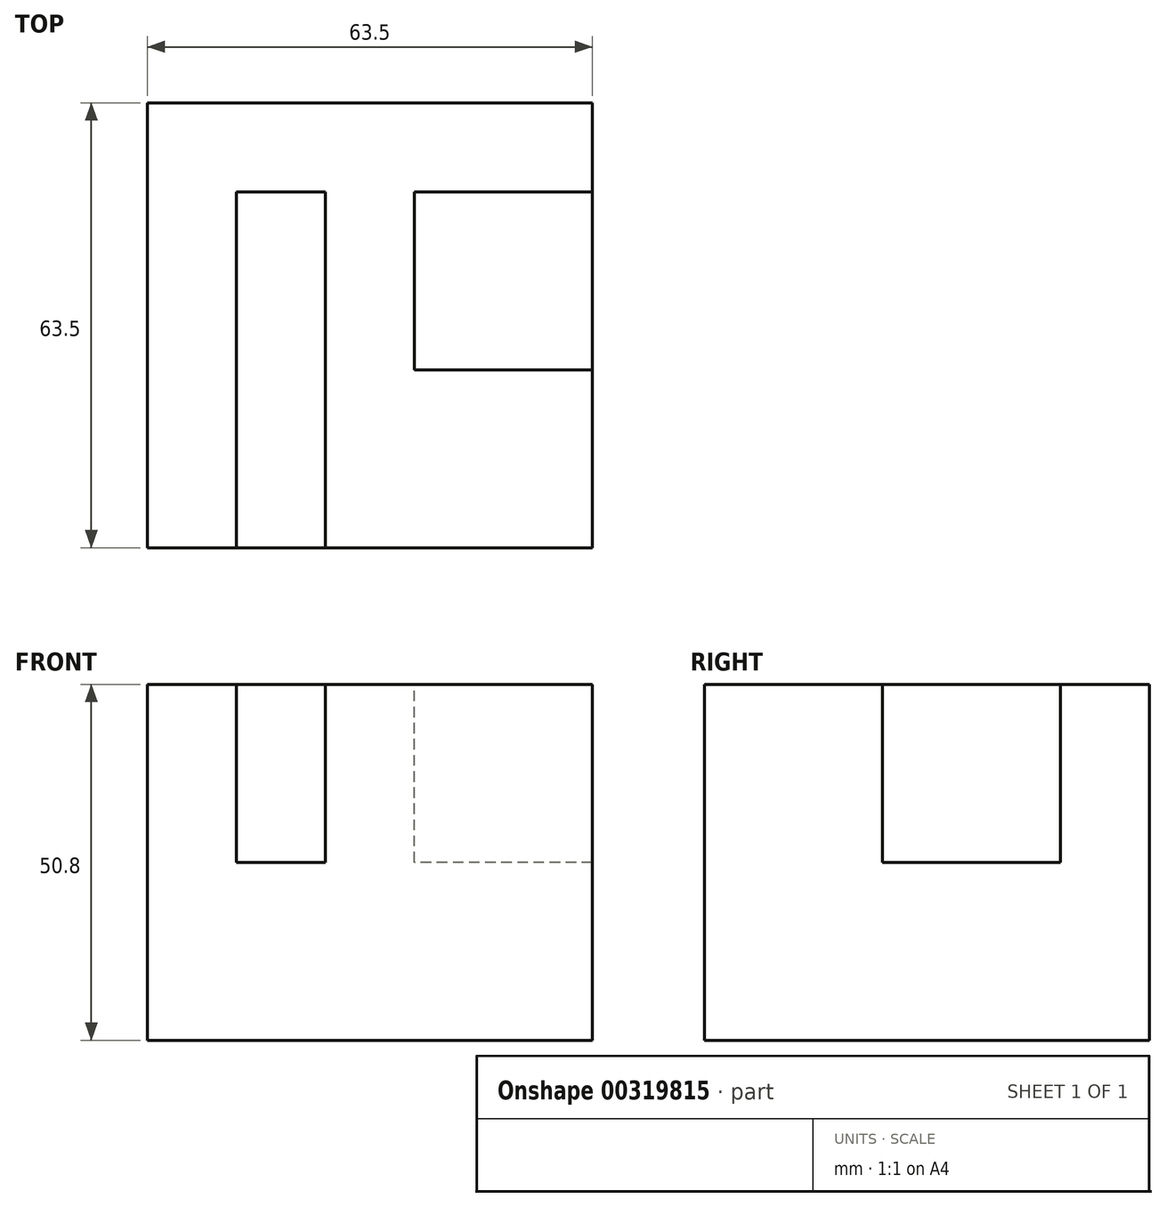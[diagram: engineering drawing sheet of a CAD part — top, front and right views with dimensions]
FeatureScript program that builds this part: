
annotation { "Feature Type Name" : "Feature", "Feature Type Description" : "" }
export const myFeature = defineFeature(function(context is Context, id is Id, definition is map)
    precondition{}
    {
        {
            var Q0;
            Q0=qCreatedBy(makeId("Top.planeOp"),FACE);
            var sketch = newSketch(context, id + "F0", { "sketchPlane" : qUnion([Q0])});
            skLineSegment(sketch, "E0.bottom", {"start": v(-38.1, 30.76) * mm, "end": v(25.4, 30.76) * mm});
            skLineSegment(sketch, "E0.top", {"start": v(-38.1, -32.74) * mm, "end": v(25.4, -32.74) * mm});
            skLineSegment(sketch, "E0.left", {"start": v(-38.1, 30.76) * mm, "end": v(-38.1, -32.74) * mm});
            skLineSegment(sketch, "E0.right", {"start": v(25.4, 30.76) * mm, "end": v(25.4, -32.74) * mm});
            skSolve(sketch);
        }
        {
            var Q0;
            Q0=makeQuery(id+"F0.imprint","IMPRINT",FACE,{"disambiguationData":[TD([[makeQuery(id+"F0.imprint","IMPRINT",EDGE,{"derivedFrom":sQuery(id+"F0.wireOp",EDGE,"E0.bottom")}),-1.0]])]});
            extrude(context, id + "F1", {"entities" : qUnion([Q0]), "oppositeDirection" : true, "depth" : 50.8 * mm});
        }
        {
            var Q0;
            Q0=makeQuery(id+"F1.opExtrude","CAP_FACE",FACE,{"disambiguationData":[OSD([sQuery(id+"F0.wireOp",EDGE,"E0.bottom"),sQuery(id+"F0.wireOp",EDGE,"E0.top"),sQuery(id+"F0.wireOp",EDGE,"E0.left"),sQuery(id+"F0.wireOp",EDGE,"E0.right")])],"isStart":true});
            var sketch = newSketch(context, id + "F2", { "sketchPlane" : qUnion([Q0])});
            skLineSegment(sketch, "E1", {"start": v(25.4, 18.06) * mm, "end": v(0, 18.06) * mm});
            skLineSegment(sketch, "E2", {"start": v(0, 18.06) * mm, "end": v(0, -7.34) * mm});
            skLineSegment(sketch, "E3", {"start": v(0, -7.34) * mm, "end": v(25.4, -7.34) * mm});
            skLineSegment(sketch, "E4", {"start": v(25.4, -7.34) * mm, "end": v(25.4, -32.74) * mm});
            skLineSegment(sketch, "E5", {"start": v(-38.1, -32.74) * mm, "end": v(-25.4, -32.74) * mm});
            skLineSegment(sketch, "E6", {"start": v(-25.4, -32.74) * mm, "end": v(-25.4, 18.06) * mm});
            skLineSegment(sketch, "E7", {"start": v(-25.4, 18.06) * mm, "end": v(-12.7, 18.06) * mm});
            skLineSegment(sketch, "E8", {"start": v(-12.7, 18.06) * mm, "end": v(-12.7, -32.74) * mm});
            skLineSegment(sketch, "E9", {"start": v(-12.7, -32.74) * mm, "end": v(-25.4, -32.74) * mm});
            skSolve(sketch);
        }
        {
            var Q0;
            Q0=makeQuery(id+"F2.imprint","IMPRINT",FACE,{"disambiguationData":[TD([[makeQuery(id+"F2.imprint","IMPRINT",EDGE,{"derivedFrom":sQuery(id+"F2.wireOp",EDGE,"E6")}),-1.0]])]});
            extrude(context, id + "F3", {"entities" : qUnion([Q0]), "operationType" : NewBodyOperationType.REMOVE, "oppositeDirection" : true, "depth" : 25.4 * mm});
        }
        {
            var Q0;
            {var subQ0=sQuery(id+"F2.wireOp",EDGE,"E1");Q0=makeQuery(id+"F2.imprint","IMPRINT",FACE,{"disambiguationData":[TD([[makeQuery(id+"F2.imprint","IMPRINT",EDGE,{"derivedFrom":subQ0}),1.0]])]});}
            extrude(context, id + "F4", {"entities" : qUnion([Q0]), "operationType" : NewBodyOperationType.REMOVE, "oppositeDirection" : true, "depth" : 25.4 * mm});
        }
    });
